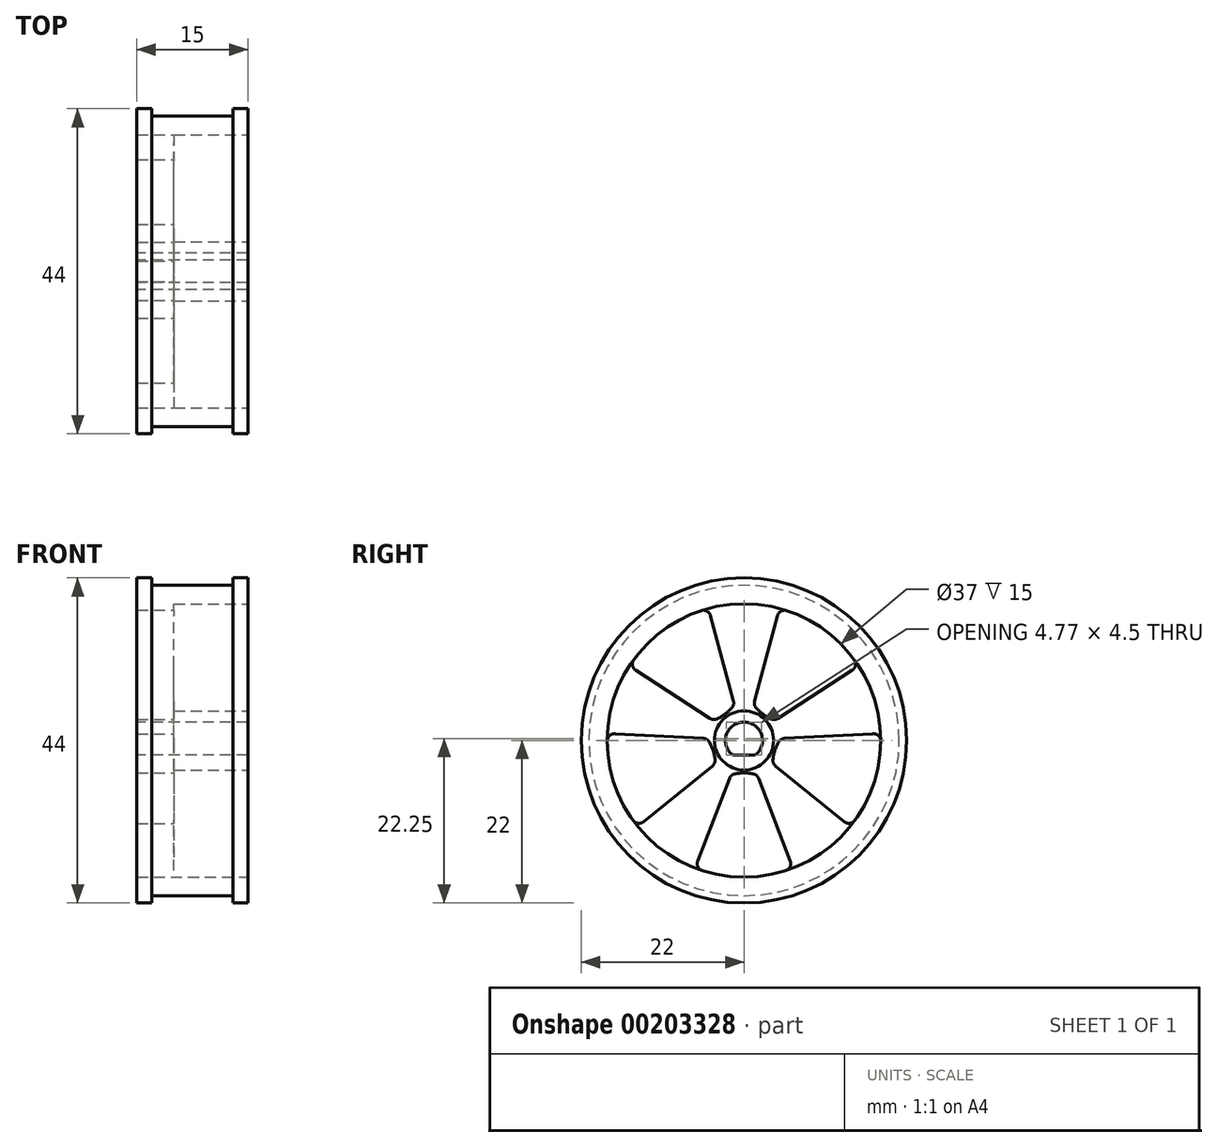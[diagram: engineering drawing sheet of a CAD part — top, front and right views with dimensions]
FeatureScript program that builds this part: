
annotation { "Feature Type Name" : "Feature", "Feature Type Description" : "" }
export const myFeature = defineFeature(function(context is Context, id is Id, definition is map)
    precondition{}
    {
        {
            var Q0;
            Q0=qCreatedBy(makeId("Right.planeOp"),FACE);
            var sketch = newSketch(context, id + "F0", { "sketchPlane" : qUnion([Q0])});
            skCircle(sketch, "E0", {"center": v(0, 0) * mm, "radius": 21 * mm});
            skSolve(sketch);
        }
        {
            var Q0;
            Q0 = qSketchRegion(id + "F0", true);
            extrude(context, id + "F1", {"entities" : qUnion([Q0]), "endBound" : BoundingType.SYMMETRIC, "depth" : 11 * mm});
        }
        {
            var Q0;
            Q0=makeQuery(id+"F1.opExtrude","CAP_FACE",FACE,{"disambiguationData":[OSD([sQuery(id+"F0.wireOp",EDGE,"E0"),sQuery(id+"F0.wireOp",EDGE,"q4wThLtx-wFus-J1GV-dAla-oBKHQIUKo1sf")])],"isStart":false});
            var sketch = newSketch(context, id + "F2", { "sketchPlane" : qUnion([Q0])});
            skCircle(sketch, "E1", {"center": v(0, 0) * mm, "radius": 22 * mm});
            skSolve(sketch);
        }
        {
            var Q0;
            Q0 = qSketchRegion(id + "F2", true);
            extrude(context, id + "F3", {"entities" : qUnion([Q0]), "operationType" : NewBodyOperationType.ADD, "depth" : 2 * mm});
        }
        {
            var Q0;
            Q0=makeQuery(id+"F1.opExtrude","CAP_FACE",FACE,{"disambiguationData":[OSD([sQuery(id+"F0.wireOp",EDGE,"E0"),sQuery(id+"F0.wireOp",EDGE,"q4wThLtx-wFus-J1GV-dAla-oBKHQIUKo1sf")])],"isStart":true});
            var sketch = newSketch(context, id + "F4", { "sketchPlane" : qUnion([Q0])});
            skCircle(sketch, "E2", {"center": v(0, 0) * mm, "radius": 22 * mm});
            skSolve(sketch);
        }
        {
            var Q0;
            Q0 = qSketchRegion(id + "F4", true);
            extrude(context, id + "F5", {"entities" : qUnion([Q0]), "operationType" : NewBodyOperationType.ADD, "depth" : 2 * mm});
        }
        {
            var Q0;
            Q0=makeQuery(id+"F5.opExtrude","CAP_FACE",FACE,{"disambiguationData":[OSD([sQuery(id+"F4.wireOp",EDGE,"E2")])],"isStart":false});
            var sketch = newSketch(context, id + "F6", { "sketchPlane" : qUnion([Q0])});
            skArc(sketch, "E3", {"start": v(1.5, -2) * mm, "mid": v(0, 2.5) * mm, "end": v(-1.5, -2) * mm});
            skLineSegment(sketch, "E4", {"start": v(1.5, -2) * mm, "end": v(-1.5, -2) * mm});
            skSolve(sketch);
        }
        {
            var Q0;
            Q0 = qSketchRegion(id + "F6", true);
            extrude(context, id + "F7", {"entities" : qUnion([Q0]), "operationType" : NewBodyOperationType.REMOVE, "endBound" : BoundingType.THROUGH_ALL, "oppositeDirection" : true, "depth" : 25 * mm});
        }
        {
            var Q0;
            Q0=makeQuery(id+"F3.opExtrude","CAP_FACE",FACE,{"disambiguationData":[OSD([sQuery(id+"F2.wireOp",EDGE,"E1")])],"isStart":false});
            var sketch = newSketch(context, id + "F8", { "sketchPlane" : qUnion([Q0])});
            skCircle(sketch, "E5", {"center": v(0, 0) * mm, "radius": 4 * mm});
            skCircle(sketch, "E6", {"center": v(0, 0) * mm, "radius": 18.5 * mm});
            skSolve(sketch);
        }
        {
            var Q0;
            Q0 = qSketchRegion(id + "F8", true);
            extrude(context, id + "F9", {"entities" : qUnion([Q0]), "operationType" : NewBodyOperationType.REMOVE, "oppositeDirection" : true, "depth" : 10 * mm});
        }
        {
            var Q0;
            Q0=makeQuery(id+"F9.boolean.opBoolean","COPY",FACE,{"derivedFrom":makeQuery(id+"F9.opExtrude","CAP_FACE",FACE,{"disambiguationData":[OSD([sQuery(id+"F8.wireOp",EDGE,"E5"),sQuery(id+"F8.wireOp",EDGE,"E6")])],"isStart":false})});
            var sketch = newSketch(context, id + "F10", { "sketchPlane" : qUnion([Q0])});
            skLineSegment(sketch, "E7", {"start": v(0, 0) * mm, "end": v(0, 18.5) * mm, "construction": true});
            skLineSegment(sketch, "E8", {"start": v(17.6, 5.72) * mm, "end": v(0, 0) * mm, "construction": true});
            skLineSegment(sketch, "E9", {"start": v(10.87, -14.97) * mm, "end": v(0, 0) * mm, "construction": true});
            skLineSegment(sketch, "E10", {"start": v(-10.87, -14.97) * mm, "end": v(0, 0) * mm, "construction": true});
            skLineSegment(sketch, "E11", {"start": v(-17.6, 5.72) * mm, "end": v(0, 0) * mm, "construction": true});
            skLineSegment(sketch, "E12", {"start": v(1.3, 4.83) * mm, "end": v(4.79, 17.87) * mm});
            skLineSegment(sketch, "E13", {"start": v(4.2, 2.72) * mm, "end": v(15.52, 10.08) * mm});
            skArc(sketch, "E14", {"start": v(4.79, 17.87) * mm, "mid": v(10.87, 14.97) * mm, "end": v(15.52, 10.08) * mm});
            skArc(sketch, "E15", {"start": v(1.3, 4.83) * mm, "mid": v(2.58, 3.55) * mm, "end": v(4.2, 2.72) * mm});
            skLineSegment(sketch, "E16.1.0", {"start": v(3.89, -3.15) * mm, "end": v(14.38, -11.64) * mm});
            skArc(sketch, "E16.1.1", {"start": v(5, 0.26) * mm, "mid": v(4.18, -1.36) * mm, "end": v(3.89, -3.15) * mm});
            skLineSegment(sketch, "E16.1.2", {"start": v(5, 0.26) * mm, "end": v(18.47, 0.97) * mm});
            skArc(sketch, "E16.1.3", {"start": v(18.47, 0.97) * mm, "mid": v(17.6, -5.72) * mm, "end": v(14.38, -11.64) * mm});
            skLineSegment(sketch, "E16.2.0", {"start": v(-1.8, -4.67) * mm, "end": v(-6.63, -17.27) * mm});
            skArc(sketch, "E16.2.1", {"start": v(1.8, -4.67) * mm, "mid": v(0, -4.4) * mm, "end": v(-1.8, -4.67) * mm});
            skLineSegment(sketch, "E16.2.2", {"start": v(1.8, -4.67) * mm, "end": v(6.63, -17.27) * mm});
            skArc(sketch, "E16.2.3", {"start": v(6.63, -17.27) * mm, "mid": v(0, -18.5) * mm, "end": v(-6.63, -17.27) * mm});
            skLineSegment(sketch, "E16.3.0", {"start": v(-5, 0.26) * mm, "end": v(-18.47, 0.97) * mm});
            skArc(sketch, "E16.3.1", {"start": v(-3.89, -3.15) * mm, "mid": v(-4.18, -1.36) * mm, "end": v(-5, 0.26) * mm});
            skLineSegment(sketch, "E16.3.2", {"start": v(-3.89, -3.15) * mm, "end": v(-14.38, -11.64) * mm});
            skArc(sketch, "E16.3.3", {"start": v(-14.38, -11.64) * mm, "mid": v(-17.6, -5.72) * mm, "end": v(-18.47, 0.97) * mm});
            skLineSegment(sketch, "E16.4.0", {"start": v(-1.3, 4.83) * mm, "end": v(-4.79, 17.87) * mm});
            skArc(sketch, "E16.4.1", {"start": v(-4.2, 2.72) * mm, "mid": v(-2.58, 3.55) * mm, "end": v(-1.3, 4.83) * mm});
            skLineSegment(sketch, "E16.4.2", {"start": v(-4.2, 2.72) * mm, "end": v(-15.52, 10.08) * mm});
            skArc(sketch, "E16.4.3", {"start": v(-15.52, 10.08) * mm, "mid": v(-10.87, 14.97) * mm, "end": v(-4.79, 17.87) * mm});
            skLineSegment(sketch, "E16.anchor1", {"start": v(0, 0) * mm, "end": v(4.2, 2.72) * mm, "construction": true});
            skLineSegment(sketch, "E16.anchor2", {"start": v(0, 0) * mm, "end": v(-1.3, 4.83) * mm, "construction": true});
            skSolve(sketch);
        }
        {
            var Q0;
            Q0 = qSketchRegion(id + "F10", true);
            extrude(context, id + "F11", {"entities" : qUnion([Q0]), "operationType" : NewBodyOperationType.REMOVE, "endBound" : BoundingType.THROUGH_ALL, "oppositeDirection" : true, "depth" : 25 * mm});
        }
        {
            var Q0;
            Q0=makeQuery(id+"F11.boolean.opBoolean","COPY",EDGE,{"derivedFrom":makeQuery(id+"F11.opExtrude","SWEPT_EDGE",EDGE,{"disambiguationData":[OSD([sQuery(id+"F10.wireOp",EDGE,"E13"),sQuery(id+"F10.wireOp",EDGE,"E15")])]})});
            var Q1;
            Q1=makeQuery(id+"F11.boolean.opBoolean","COPY",EDGE,{"derivedFrom":makeQuery(id+"F11.opExtrude","SWEPT_EDGE",EDGE,{"disambiguationData":[OSD([sQuery(id+"F10.wireOp",EDGE,"E12"),sQuery(id+"F10.wireOp",EDGE,"E15")])]})});
            var Q2;
            Q2=makeQuery(id+"F11.boolean.opBoolean","COPY",EDGE,{"derivedFrom":makeQuery(id+"F11.opExtrude","SWEPT_EDGE",EDGE,{"disambiguationData":[OSD([sQuery(id+"F8.wireOp",EDGE,"E6"),sQuery(id+"F10.wireOp",EDGE,"E13"),sQuery(id+"F10.wireOp",EDGE,"E14")])]})});
            var Q3;
            Q3=makeQuery(id+"F11.boolean.opBoolean","COPY",EDGE,{"derivedFrom":makeQuery(id+"F11.opExtrude","SWEPT_EDGE",EDGE,{"disambiguationData":[OSD([sQuery(id+"F8.wireOp",EDGE,"E6"),sQuery(id+"F10.wireOp",EDGE,"E12"),sQuery(id+"F10.wireOp",EDGE,"E14")])]})});
            var Q4;
            Q4=makeQuery(id+"F11.boolean.opBoolean","COPY",EDGE,{"derivedFrom":makeQuery(id+"F11.opExtrude","SWEPT_EDGE",EDGE,{"disambiguationData":[OSD([sQuery(id+"F10.wireOp",EDGE,"E16.1.1"),sQuery(id+"F10.wireOp",EDGE,"E16.1.2")])]})});
            var Q5;
            Q5=makeQuery(id+"F11.boolean.opBoolean","COPY",EDGE,{"derivedFrom":makeQuery(id+"F11.opExtrude","SWEPT_EDGE",EDGE,{"disambiguationData":[OSD([sQuery(id+"F10.wireOp",EDGE,"E16.1.0"),sQuery(id+"F10.wireOp",EDGE,"E16.1.1")])]})});
            var Q6;
            Q6=makeQuery(id+"F11.boolean.opBoolean","COPY",EDGE,{"derivedFrom":makeQuery(id+"F11.opExtrude","SWEPT_EDGE",EDGE,{"disambiguationData":[OSD([sQuery(id+"F10.wireOp",EDGE,"E16.2.1"),sQuery(id+"F10.wireOp",EDGE,"E16.2.2")])]})});
            var Q7;
            Q7=makeQuery(id+"F11.boolean.opBoolean","COPY",EDGE,{"derivedFrom":makeQuery(id+"F11.opExtrude","SWEPT_EDGE",EDGE,{"disambiguationData":[OSD([sQuery(id+"F10.wireOp",EDGE,"E16.2.0"),sQuery(id+"F10.wireOp",EDGE,"E16.2.1")])]})});
            var Q8;
            Q8=makeQuery(id+"F11.boolean.opBoolean","COPY",EDGE,{"derivedFrom":makeQuery(id+"F11.opExtrude","SWEPT_EDGE",EDGE,{"disambiguationData":[OSD([sQuery(id+"F10.wireOp",EDGE,"E16.3.0"),sQuery(id+"F10.wireOp",EDGE,"E16.3.1")])]})});
            var Q9;
            Q9=makeQuery(id+"F11.boolean.opBoolean","COPY",EDGE,{"derivedFrom":makeQuery(id+"F11.opExtrude","SWEPT_EDGE",EDGE,{"disambiguationData":[OSD([sQuery(id+"F10.wireOp",EDGE,"E16.3.1"),sQuery(id+"F10.wireOp",EDGE,"E16.3.2")])]})});
            var Q10;
            Q10=makeQuery(id+"F11.boolean.opBoolean","COPY",EDGE,{"derivedFrom":makeQuery(id+"F11.opExtrude","SWEPT_EDGE",EDGE,{"disambiguationData":[OSD([sQuery(id+"F10.wireOp",EDGE,"E16.4.1"),sQuery(id+"F10.wireOp",EDGE,"E16.4.2")])]})});
            var Q11;
            Q11=makeQuery(id+"F11.boolean.opBoolean","COPY",EDGE,{"derivedFrom":makeQuery(id+"F11.opExtrude","SWEPT_EDGE",EDGE,{"disambiguationData":[OSD([sQuery(id+"F10.wireOp",EDGE,"E16.4.0"),sQuery(id+"F10.wireOp",EDGE,"E16.4.1")])]})});
            var Q12;
            Q12=makeQuery(id+"F11.boolean.opBoolean","COPY",EDGE,{"derivedFrom":makeQuery(id+"F11.opExtrude","SWEPT_EDGE",EDGE,{"disambiguationData":[OSD([sQuery(id+"F8.wireOp",EDGE,"E6"),sQuery(id+"F10.wireOp",EDGE,"E16.1.0"),sQuery(id+"F10.wireOp",EDGE,"E16.1.3")])]})});
            var Q13;
            Q13=makeQuery(id+"F11.boolean.opBoolean","COPY",EDGE,{"derivedFrom":makeQuery(id+"F11.opExtrude","SWEPT_EDGE",EDGE,{"disambiguationData":[OSD([sQuery(id+"F8.wireOp",EDGE,"E6"),sQuery(id+"F10.wireOp",EDGE,"E16.1.2"),sQuery(id+"F10.wireOp",EDGE,"E16.1.3")])]})});
            var Q14;
            Q14=makeQuery(id+"F11.boolean.opBoolean","COPY",EDGE,{"derivedFrom":makeQuery(id+"F11.opExtrude","SWEPT_EDGE",EDGE,{"disambiguationData":[OSD([sQuery(id+"F8.wireOp",EDGE,"E6"),sQuery(id+"F10.wireOp",EDGE,"E16.2.2"),sQuery(id+"F10.wireOp",EDGE,"E16.2.3")])]})});
            var Q15;
            Q15=makeQuery(id+"F11.boolean.opBoolean","COPY",EDGE,{"derivedFrom":makeQuery(id+"F11.opExtrude","SWEPT_EDGE",EDGE,{"disambiguationData":[OSD([sQuery(id+"F8.wireOp",EDGE,"E6"),sQuery(id+"F10.wireOp",EDGE,"E16.2.0"),sQuery(id+"F10.wireOp",EDGE,"E16.2.3")])]})});
            var Q16;
            Q16=makeQuery(id+"F11.boolean.opBoolean","COPY",EDGE,{"derivedFrom":makeQuery(id+"F11.opExtrude","SWEPT_EDGE",EDGE,{"disambiguationData":[OSD([sQuery(id+"F8.wireOp",EDGE,"E6"),sQuery(id+"F10.wireOp",EDGE,"E16.3.0"),sQuery(id+"F10.wireOp",EDGE,"E16.3.3")])]})});
            var Q17;
            Q17=makeQuery(id+"F11.boolean.opBoolean","COPY",EDGE,{"derivedFrom":makeQuery(id+"F11.opExtrude","SWEPT_EDGE",EDGE,{"disambiguationData":[OSD([sQuery(id+"F8.wireOp",EDGE,"E6"),sQuery(id+"F10.wireOp",EDGE,"E16.3.2"),sQuery(id+"F10.wireOp",EDGE,"E16.3.3")])]})});
            var Q18;
            Q18=makeQuery(id+"F11.boolean.opBoolean","COPY",EDGE,{"derivedFrom":makeQuery(id+"F11.opExtrude","SWEPT_EDGE",EDGE,{"disambiguationData":[OSD([sQuery(id+"F8.wireOp",EDGE,"E6"),sQuery(id+"F10.wireOp",EDGE,"E16.4.0"),sQuery(id+"F10.wireOp",EDGE,"E16.4.3")])]})});
            var Q19;
            Q19=makeQuery(id+"F11.boolean.opBoolean","COPY",EDGE,{"derivedFrom":makeQuery(id+"F11.opExtrude","SWEPT_EDGE",EDGE,{"disambiguationData":[OSD([sQuery(id+"F8.wireOp",EDGE,"E6"),sQuery(id+"F10.wireOp",EDGE,"E16.4.2"),sQuery(id+"F10.wireOp",EDGE,"E16.4.3")])]})});
            fillet(context, id + "F12", {"entities" : qUnion([Q0, Q1, Q2, Q3, Q4, Q5, Q6, Q7, Q8, Q9, Q10, Q11, Q12, Q13, Q14, Q15, Q16, Q17, Q18, Q19]), "radius" : 1 * mm, "tangentPropagation" : true, "allowEdgeOverflow" : false});
        }
    });
